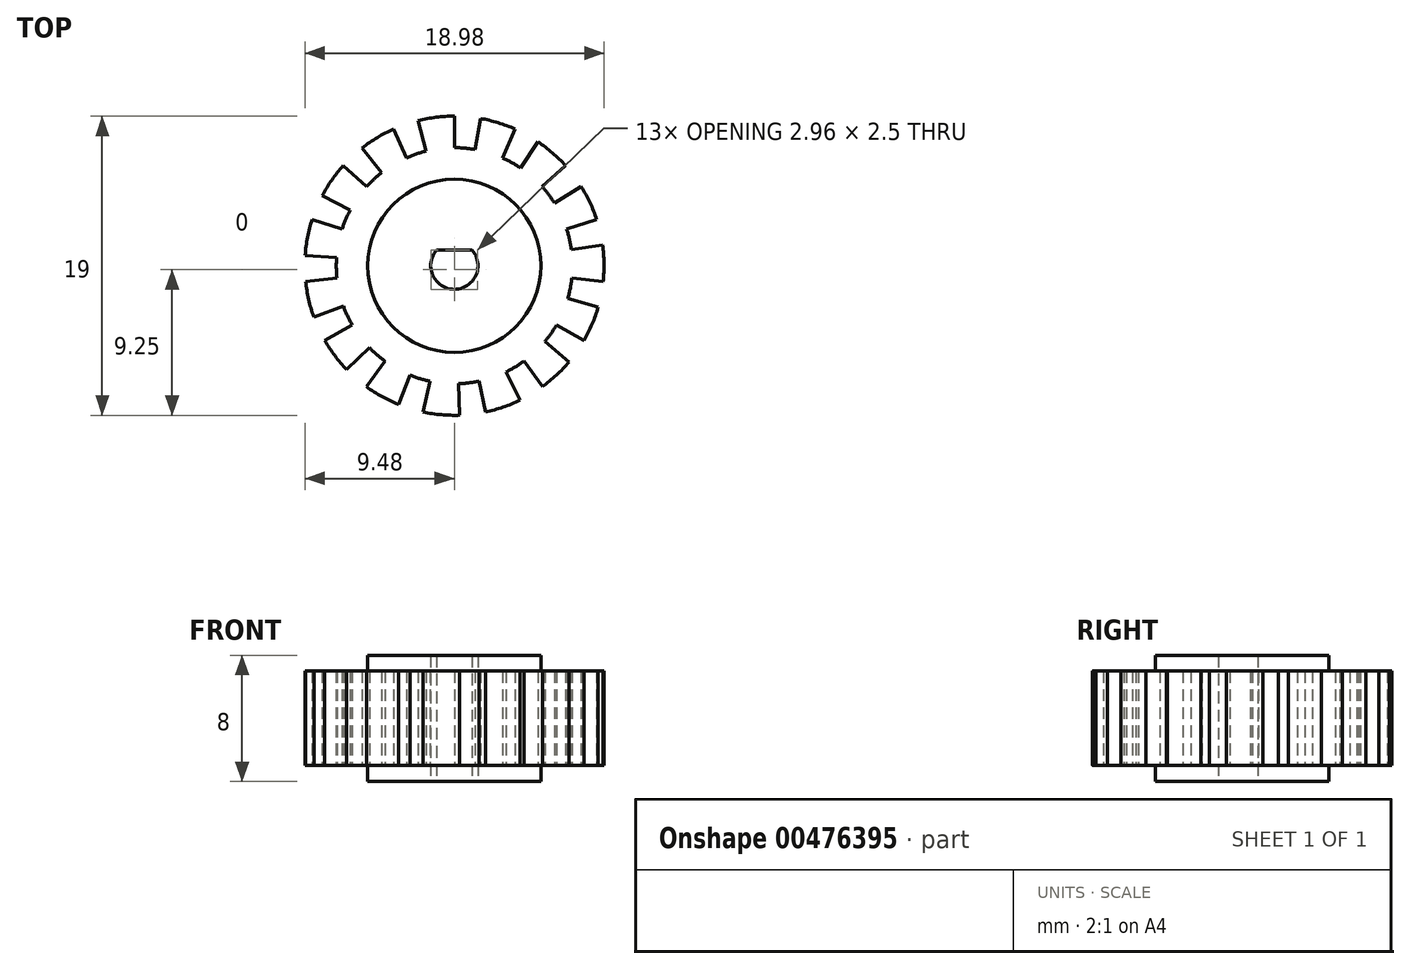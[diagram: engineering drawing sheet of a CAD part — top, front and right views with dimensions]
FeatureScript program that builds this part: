
annotation { "Feature Type Name" : "Feature", "Feature Type Description" : "" }
export const myFeature = defineFeature(function(context is Context, id is Id, definition is map)
    precondition{}
    {
        {
            var Q0;
            Q0=qCreatedBy(makeId("Top.planeOp"),FACE);
            var sketch = newSketch(context, id + "F0", { "sketchPlane" : qUnion([Q0])});
            skArc(sketch, "E0", {"start": v(0, 9.5) * mm, "mid": v(-1.16, 9.43) * mm, "end": v(-2.3, 9.22) * mm});
            skArc(sketch, "E1", {"start": v(-1.81, 7.28) * mm, "mid": v(-2.44, 7.1) * mm, "end": v(-3.05, 6.85) * mm});
            skLineSegment(sketch, "E2", {"start": v(-2.3, 9.22) * mm, "end": v(-1.81, 7.28) * mm});
            skLineSegment(sketch, "E3", {"start": v(0, 9.5) * mm, "end": v(0, 7.5) * mm});
            skLineSegment(sketch, "E4", {"start": v(-1.81, 7.28) * mm, "end": v(0, 0) * mm, "construction": true});
            skLineSegment(sketch, "E5", {"start": v(0, 7.5) * mm, "end": v(0, 0) * mm, "construction": true});
            skLineSegment(sketch, "E6", {"start": v(0, 0) * mm, "end": v(-3.05, 6.85) * mm, "construction": true});
            skArc(sketch, "E7.1.0", {"start": v(-4.62, 5.91) * mm, "mid": v(-5.11, 5.49) * mm, "end": v(-5.57, 5.02) * mm});
            skLineSegment(sketch, "E7.1.1", {"start": v(-5.85, 7.49) * mm, "end": v(-4.62, 5.91) * mm});
            skArc(sketch, "E7.1.2", {"start": v(-3.86, 8.68) * mm, "mid": v(-4.9, 8.14) * mm, "end": v(-5.85, 7.49) * mm});
            skLineSegment(sketch, "E7.1.3", {"start": v(-3.86, 8.68) * mm, "end": v(-3.05, 6.85) * mm});
            skArc(sketch, "E7.2.0", {"start": v(-6.62, 3.52) * mm, "mid": v(-6.9, 2.93) * mm, "end": v(-7.13, 2.32) * mm});
            skLineSegment(sketch, "E7.2.1", {"start": v(-8.39, 4.46) * mm, "end": v(-6.62, 3.52) * mm});
            skArc(sketch, "E7.2.2", {"start": v(-7.06, 6.36) * mm, "mid": v(-7.78, 5.45) * mm, "end": v(-8.39, 4.46) * mm});
            skLineSegment(sketch, "E7.2.3", {"start": v(-7.06, 6.36) * mm, "end": v(-5.57, 5.02) * mm});
            skArc(sketch, "E7.3.0", {"start": v(-7.48, 0.52) * mm, "mid": v(-7.5, -0.13) * mm, "end": v(-7.46, -0.78) * mm});
            skLineSegment(sketch, "E7.3.1", {"start": v(-9.48, 0.66) * mm, "end": v(-7.48, 0.52) * mm});
            skArc(sketch, "E7.3.2", {"start": v(-9.04, 2.94) * mm, "mid": v(-9.33, 1.81) * mm, "end": v(-9.48, 0.66) * mm});
            skLineSegment(sketch, "E7.3.3", {"start": v(-9.04, 2.94) * mm, "end": v(-7.13, 2.32) * mm});
            skArc(sketch, "E7.4.0", {"start": v(-7.05, -2.57) * mm, "mid": v(-6.8, -3.17) * mm, "end": v(-6.5, -3.75) * mm});
            skLineSegment(sketch, "E7.4.1", {"start": v(-8.93, -3.25) * mm, "end": v(-7.05, -2.57) * mm});
            skArc(sketch, "E7.4.2", {"start": v(-9.45, -1) * mm, "mid": v(-9.26, -2.14) * mm, "end": v(-8.93, -3.25) * mm});
            skLineSegment(sketch, "E7.4.3", {"start": v(-9.45, -1) * mm, "end": v(-7.46, -0.78) * mm});
            skArc(sketch, "E7.5.0", {"start": v(-5.4, -5.2) * mm, "mid": v(-4.92, -5.66) * mm, "end": v(-4.4, -6.07) * mm});
            skLineSegment(sketch, "E7.5.1", {"start": v(-6.83, -6.6) * mm, "end": v(-5.4, -5.2) * mm});
            skArc(sketch, "E7.5.2", {"start": v(-8.23, -4.75) * mm, "mid": v(-7.59, -5.72) * mm, "end": v(-6.83, -6.6) * mm});
            skLineSegment(sketch, "E7.5.3", {"start": v(-8.23, -4.75) * mm, "end": v(-6.5, -3.75) * mm});
            skArc(sketch, "E7.6.0", {"start": v(-2.8, -6.95) * mm, "mid": v(-2.2, -7.17) * mm, "end": v(-1.56, -7.34) * mm});
            skLineSegment(sketch, "E7.6.1", {"start": v(-3.56, -8.8) * mm, "end": v(-2.8, -6.95) * mm});
            skArc(sketch, "E7.6.2", {"start": v(-5.58, -7.69) * mm, "mid": v(-4.6, -8.3) * mm, "end": v(-3.56, -8.8) * mm});
            skLineSegment(sketch, "E7.6.3", {"start": v(-5.58, -7.69) * mm, "end": v(-4.4, -6.07) * mm});
            skArc(sketch, "E7.7.0", {"start": v(0.26, -7.5) * mm, "mid": v(0.91, -7.44) * mm, "end": v(1.56, -7.34) * mm});
            skLineSegment(sketch, "E7.7.1", {"start": v(0.33, -9.5) * mm, "end": v(0.26, -7.5) * mm});
            skArc(sketch, "E7.7.2", {"start": v(-1.98, -9.3) * mm, "mid": v(-0.83, -9.46) * mm, "end": v(0.33, -9.5) * mm});
            skLineSegment(sketch, "E7.7.3", {"start": v(-1.98, -9.3) * mm, "end": v(-1.56, -7.34) * mm});
            skArc(sketch, "E7.8.0", {"start": v(3.29, -6.74) * mm, "mid": v(3.86, -6.43) * mm, "end": v(4.4, -6.07) * mm});
            skLineSegment(sketch, "E7.8.1", {"start": v(4.16, -8.54) * mm, "end": v(3.29, -6.74) * mm});
            skArc(sketch, "E7.8.2", {"start": v(1.98, -9.3) * mm, "mid": v(3.1, -8.98) * mm, "end": v(4.16, -8.54) * mm});
            skLineSegment(sketch, "E7.8.3", {"start": v(1.98, -9.3) * mm, "end": v(1.56, -7.34) * mm});
            skArc(sketch, "E7.9.0", {"start": v(5.75, -4.82) * mm, "mid": v(6.14, -4.3) * mm, "end": v(6.5, -3.75) * mm});
            skLineSegment(sketch, "E7.9.1", {"start": v(7.28, -6.1) * mm, "end": v(5.75, -4.82) * mm});
            skArc(sketch, "E7.9.2", {"start": v(5.58, -7.69) * mm, "mid": v(6.48, -6.95) * mm, "end": v(7.28, -6.1) * mm});
            skLineSegment(sketch, "E7.9.3", {"start": v(5.58, -7.69) * mm, "end": v(4.4, -6.07) * mm});
            skArc(sketch, "E7.10.0", {"start": v(7.2, -2.07) * mm, "mid": v(7.36, -1.43) * mm, "end": v(7.46, -0.78) * mm});
            skLineSegment(sketch, "E7.10.1", {"start": v(9.13, -2.62) * mm, "end": v(7.2, -2.07) * mm});
            skArc(sketch, "E7.10.2", {"start": v(8.23, -4.75) * mm, "mid": v(8.74, -3.71) * mm, "end": v(9.13, -2.62) * mm});
            skLineSegment(sketch, "E7.10.3", {"start": v(8.23, -4.75) * mm, "end": v(6.5, -3.75) * mm});
            skArc(sketch, "E7.11.0", {"start": v(7.43, 1.04) * mm, "mid": v(7.3, 1.69) * mm, "end": v(7.13, 2.32) * mm});
            skLineSegment(sketch, "E7.11.1", {"start": v(9.4, 1.32) * mm, "end": v(7.43, 1.04) * mm});
            skArc(sketch, "E7.11.2", {"start": v(9.45, -1) * mm, "mid": v(9.5, 0.17) * mm, "end": v(9.4, 1.32) * mm});
            skLineSegment(sketch, "E7.11.3", {"start": v(9.45, -1) * mm, "end": v(7.46, -0.78) * mm});
            skArc(sketch, "E7.12.0", {"start": v(6.36, 3.97) * mm, "mid": v(5.99, 4.51) * mm, "end": v(5.57, 5.02) * mm});
            skLineSegment(sketch, "E7.12.1", {"start": v(8.06, 5.03) * mm, "end": v(6.36, 3.97) * mm});
            skArc(sketch, "E7.12.2", {"start": v(9.04, 2.94) * mm, "mid": v(8.6, 4.01) * mm, "end": v(8.06, 5.03) * mm});
            skLineSegment(sketch, "E7.12.3", {"start": v(9.04, 2.94) * mm, "end": v(7.13, 2.32) * mm});
            skArc(sketch, "E7.13.0", {"start": v(4.2, 6.22) * mm, "mid": v(3.64, 6.56) * mm, "end": v(3.05, 6.85) * mm});
            skLineSegment(sketch, "E7.13.1", {"start": v(5.31, 7.88) * mm, "end": v(4.2, 6.22) * mm});
            skArc(sketch, "E7.13.2", {"start": v(7.06, 6.36) * mm, "mid": v(6.23, 7.17) * mm, "end": v(5.31, 7.88) * mm});
            skLineSegment(sketch, "E7.13.3", {"start": v(7.06, 6.36) * mm, "end": v(5.57, 5.02) * mm});
            skArc(sketch, "E7.14.0", {"start": v(1.3, 7.39) * mm, "mid": v(0.65, 7.47) * mm, "end": v(0, 7.5) * mm});
            skLineSegment(sketch, "E7.14.1", {"start": v(1.65, 9.36) * mm, "end": v(1.3, 7.39) * mm});
            skArc(sketch, "E7.14.2", {"start": v(3.86, 8.68) * mm, "mid": v(2.78, 9.08) * mm, "end": v(1.65, 9.36) * mm});
            skLineSegment(sketch, "E7.14.3", {"start": v(3.86, 8.68) * mm, "end": v(3.05, 6.85) * mm});
            skArc(sketch, "E8", {"start": v(-1.12, 1) * mm, "mid": v(0, -1.5) * mm, "end": v(1.12, 1) * mm});
            skLineSegment(sketch, "E9", {"start": v(-1.12, 1) * mm, "end": v(1.12, 1) * mm});
            skSolve(sketch);
        }
        {
            var Q0;
            Q0=makeQuery(id+"F0.imprint","IMPRINT",FACE,{"disambiguationData":[TD([[makeQuery(id+"F0.imprint","IMPRINT",EDGE,{"derivedFrom":sQuery(id+"F0.wireOp",EDGE,"E0")}),1.0]])]});
            extrude(context, id + "F1", {"entities" : qUnion([Q0]), "depth" : 8 * mm});
        }
        {
            var Q0;
            Q0=makeQuery(id+"F1.opExtrude","CAP_FACE",FACE,{"disambiguationData":[OSD([sQuery(id+"F0.wireOp",EDGE,"E0"),sQuery(id+"F0.wireOp",EDGE,"E1"),sQuery(id+"F0.wireOp",EDGE,"E2"),sQuery(id+"F0.wireOp",EDGE,"E3"),sQuery(id+"F0.wireOp",EDGE,"E7.1.0"),sQuery(id+"F0.wireOp",EDGE,"E7.1.1"),sQuery(id+"F0.wireOp",EDGE,"E7.1.2"),sQuery(id+"F0.wireOp",EDGE,"E7.1.3"),sQuery(id+"F0.wireOp",EDGE,"E7.2.0"),sQuery(id+"F0.wireOp",EDGE,"E7.2.1"),sQuery(id+"F0.wireOp",EDGE,"E7.2.2"),sQuery(id+"F0.wireOp",EDGE,"E7.2.3"),sQuery(id+"F0.wireOp",EDGE,"E7.3.0"),sQuery(id+"F0.wireOp",EDGE,"E7.3.1"),sQuery(id+"F0.wireOp",EDGE,"E7.3.2"),sQuery(id+"F0.wireOp",EDGE,"E7.3.3"),sQuery(id+"F0.wireOp",EDGE,"E7.4.0"),sQuery(id+"F0.wireOp",EDGE,"E7.4.1"),sQuery(id+"F0.wireOp",EDGE,"E7.4.2"),sQuery(id+"F0.wireOp",EDGE,"E7.4.3"),sQuery(id+"F0.wireOp",EDGE,"E7.5.0"),sQuery(id+"F0.wireOp",EDGE,"E7.5.1"),sQuery(id+"F0.wireOp",EDGE,"E7.5.2"),sQuery(id+"F0.wireOp",EDGE,"E7.5.3"),sQuery(id+"F0.wireOp",EDGE,"E7.6.0"),sQuery(id+"F0.wireOp",EDGE,"E7.6.1"),sQuery(id+"F0.wireOp",EDGE,"E7.6.2"),sQuery(id+"F0.wireOp",EDGE,"E7.6.3"),sQuery(id+"F0.wireOp",EDGE,"E7.7.0"),sQuery(id+"F0.wireOp",EDGE,"E7.7.1"),sQuery(id+"F0.wireOp",EDGE,"E7.7.2"),sQuery(id+"F0.wireOp",EDGE,"E7.7.3"),sQuery(id+"F0.wireOp",EDGE,"E7.8.0"),sQuery(id+"F0.wireOp",EDGE,"E7.8.1"),sQuery(id+"F0.wireOp",EDGE,"E7.8.2"),sQuery(id+"F0.wireOp",EDGE,"E7.8.3"),sQuery(id+"F0.wireOp",EDGE,"E7.9.0"),sQuery(id+"F0.wireOp",EDGE,"E7.9.1"),sQuery(id+"F0.wireOp",EDGE,"E7.9.2"),sQuery(id+"F0.wireOp",EDGE,"E7.9.3"),sQuery(id+"F0.wireOp",EDGE,"E7.10.0"),sQuery(id+"F0.wireOp",EDGE,"E7.10.1"),sQuery(id+"F0.wireOp",EDGE,"E7.10.2"),sQuery(id+"F0.wireOp",EDGE,"E7.10.3"),sQuery(id+"F0.wireOp",EDGE,"E7.11.0"),sQuery(id+"F0.wireOp",EDGE,"E7.11.1"),sQuery(id+"F0.wireOp",EDGE,"E7.11.2"),sQuery(id+"F0.wireOp",EDGE,"E7.11.3"),sQuery(id+"F0.wireOp",EDGE,"E7.12.0"),sQuery(id+"F0.wireOp",EDGE,"E7.12.1"),sQuery(id+"F0.wireOp",EDGE,"E7.12.2"),sQuery(id+"F0.wireOp",EDGE,"E7.12.3"),sQuery(id+"F0.wireOp",EDGE,"E7.13.0"),sQuery(id+"F0.wireOp",EDGE,"E7.13.1"),sQuery(id+"F0.wireOp",EDGE,"E7.13.2"),sQuery(id+"F0.wireOp",EDGE,"E7.13.3"),sQuery(id+"F0.wireOp",EDGE,"E7.14.0"),sQuery(id+"F0.wireOp",EDGE,"E7.14.1"),sQuery(id+"F0.wireOp",EDGE,"E7.14.2"),sQuery(id+"F0.wireOp",EDGE,"E7.14.3"),sQuery(id+"F0.wireOp",EDGE,"E8"),sQuery(id+"F0.wireOp",EDGE,"E9")])],"isStart":false});
            var sketch = newSketch(context, id + "F2", { "sketchPlane" : qUnion([Q0])});
            skCircle(sketch, "E10", {"center": v(0, 0) * mm, "radius": 5.5 * mm});
            skCircle(sketch, "E11", {"center": v(0, 0) * mm, "radius": 9.5 * mm});
            skSolve(sketch);
        }
        {
            var Q0;
            Q0=qSketchRegion(id+"F2",true);
            extrude(context, id + "F3", {"entities" : qUnion([Q0]), "operationType" : NewBodyOperationType.REMOVE, "oppositeDirection" : true, "depth" : 1 * mm});
        }
        {
            var Q0;
            Q0=makeQuery(id+"F1.opExtrude","CAP_FACE",FACE,{"disambiguationData":[OSD([sQuery(id+"F0.wireOp",EDGE,"E0"),sQuery(id+"F0.wireOp",EDGE,"E1"),sQuery(id+"F0.wireOp",EDGE,"E2"),sQuery(id+"F0.wireOp",EDGE,"E3"),sQuery(id+"F0.wireOp",EDGE,"E7.1.0"),sQuery(id+"F0.wireOp",EDGE,"E7.1.1"),sQuery(id+"F0.wireOp",EDGE,"E7.1.2"),sQuery(id+"F0.wireOp",EDGE,"E7.1.3"),sQuery(id+"F0.wireOp",EDGE,"E7.2.0"),sQuery(id+"F0.wireOp",EDGE,"E7.2.1"),sQuery(id+"F0.wireOp",EDGE,"E7.2.2"),sQuery(id+"F0.wireOp",EDGE,"E7.2.3"),sQuery(id+"F0.wireOp",EDGE,"E7.3.0"),sQuery(id+"F0.wireOp",EDGE,"E7.3.1"),sQuery(id+"F0.wireOp",EDGE,"E7.3.2"),sQuery(id+"F0.wireOp",EDGE,"E7.3.3"),sQuery(id+"F0.wireOp",EDGE,"E7.4.0"),sQuery(id+"F0.wireOp",EDGE,"E7.4.1"),sQuery(id+"F0.wireOp",EDGE,"E7.4.2"),sQuery(id+"F0.wireOp",EDGE,"E7.4.3"),sQuery(id+"F0.wireOp",EDGE,"E7.5.0"),sQuery(id+"F0.wireOp",EDGE,"E7.5.1"),sQuery(id+"F0.wireOp",EDGE,"E7.5.2"),sQuery(id+"F0.wireOp",EDGE,"E7.5.3"),sQuery(id+"F0.wireOp",EDGE,"E7.6.0"),sQuery(id+"F0.wireOp",EDGE,"E7.6.1"),sQuery(id+"F0.wireOp",EDGE,"E7.6.2"),sQuery(id+"F0.wireOp",EDGE,"E7.6.3"),sQuery(id+"F0.wireOp",EDGE,"E7.7.0"),sQuery(id+"F0.wireOp",EDGE,"E7.7.1"),sQuery(id+"F0.wireOp",EDGE,"E7.7.2"),sQuery(id+"F0.wireOp",EDGE,"E7.7.3"),sQuery(id+"F0.wireOp",EDGE,"E7.8.0"),sQuery(id+"F0.wireOp",EDGE,"E7.8.1"),sQuery(id+"F0.wireOp",EDGE,"E7.8.2"),sQuery(id+"F0.wireOp",EDGE,"E7.8.3"),sQuery(id+"F0.wireOp",EDGE,"E7.9.0"),sQuery(id+"F0.wireOp",EDGE,"E7.9.1"),sQuery(id+"F0.wireOp",EDGE,"E7.9.2"),sQuery(id+"F0.wireOp",EDGE,"E7.9.3"),sQuery(id+"F0.wireOp",EDGE,"E7.10.0"),sQuery(id+"F0.wireOp",EDGE,"E7.10.1"),sQuery(id+"F0.wireOp",EDGE,"E7.10.2"),sQuery(id+"F0.wireOp",EDGE,"E7.10.3"),sQuery(id+"F0.wireOp",EDGE,"E7.11.0"),sQuery(id+"F0.wireOp",EDGE,"E7.11.1"),sQuery(id+"F0.wireOp",EDGE,"E7.11.2"),sQuery(id+"F0.wireOp",EDGE,"E7.11.3"),sQuery(id+"F0.wireOp",EDGE,"E7.12.0"),sQuery(id+"F0.wireOp",EDGE,"E7.12.1"),sQuery(id+"F0.wireOp",EDGE,"E7.12.2"),sQuery(id+"F0.wireOp",EDGE,"E7.12.3"),sQuery(id+"F0.wireOp",EDGE,"E7.13.0"),sQuery(id+"F0.wireOp",EDGE,"E7.13.1"),sQuery(id+"F0.wireOp",EDGE,"E7.13.2"),sQuery(id+"F0.wireOp",EDGE,"E7.13.3"),sQuery(id+"F0.wireOp",EDGE,"E7.14.0"),sQuery(id+"F0.wireOp",EDGE,"E7.14.1"),sQuery(id+"F0.wireOp",EDGE,"E7.14.2"),sQuery(id+"F0.wireOp",EDGE,"E7.14.3"),sQuery(id+"F0.wireOp",EDGE,"E8"),sQuery(id+"F0.wireOp",EDGE,"E9")])],"isStart":true});
            var sketch = newSketch(context, id + "F4", { "sketchPlane" : qUnion([Q0])});
            skCircle(sketch, "E12", {"center": v(0, 0) * mm, "radius": 9.5 * mm});
            skCircle(sketch, "E13", {"center": v(0, 0) * mm, "radius": 5.5 * mm});
            skSolve(sketch);
        }
        {
            var Q0;
            Q0=qSketchRegion(id+"F4",true);
            extrude(context, id + "F5", {"entities" : qUnion([Q0]), "operationType" : NewBodyOperationType.REMOVE, "oppositeDirection" : true, "depth" : 1 * mm});
        }
    });
